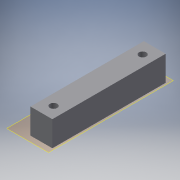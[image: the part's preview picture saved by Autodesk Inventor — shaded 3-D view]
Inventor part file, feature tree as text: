
AUTODESK INVENTOR PART (.ipt)
format: ipt  version: 2017 (Build 210142000, 142)  size: 100,864 bytes
history: native  units: mm
features: other x7, extrude x1, sketch x1
ambient origin geometry x8: Origin, YZ Plane, XZ Plane, XY Plane, X Axis, Y Axis, Z Axis, Center Point
bodies: Solide1 (feature_tree)
feature tree (9):
  other  "Plan de construction1"
  extrude  "Extrusion1"  Depth=15.5mm TaperAngle=0.0deg
  sketch  "Esquisse1"
  other  "Référence1"
  other  "Référence2"
  other  "<userpath>\Documents\Modele 3D\Lanceur boule\Ensemble_Lanceur.iam"
  other  "Ensemble_Lanceur.iam"
  other  "enclenchement:1"
  other  "aret:1"
